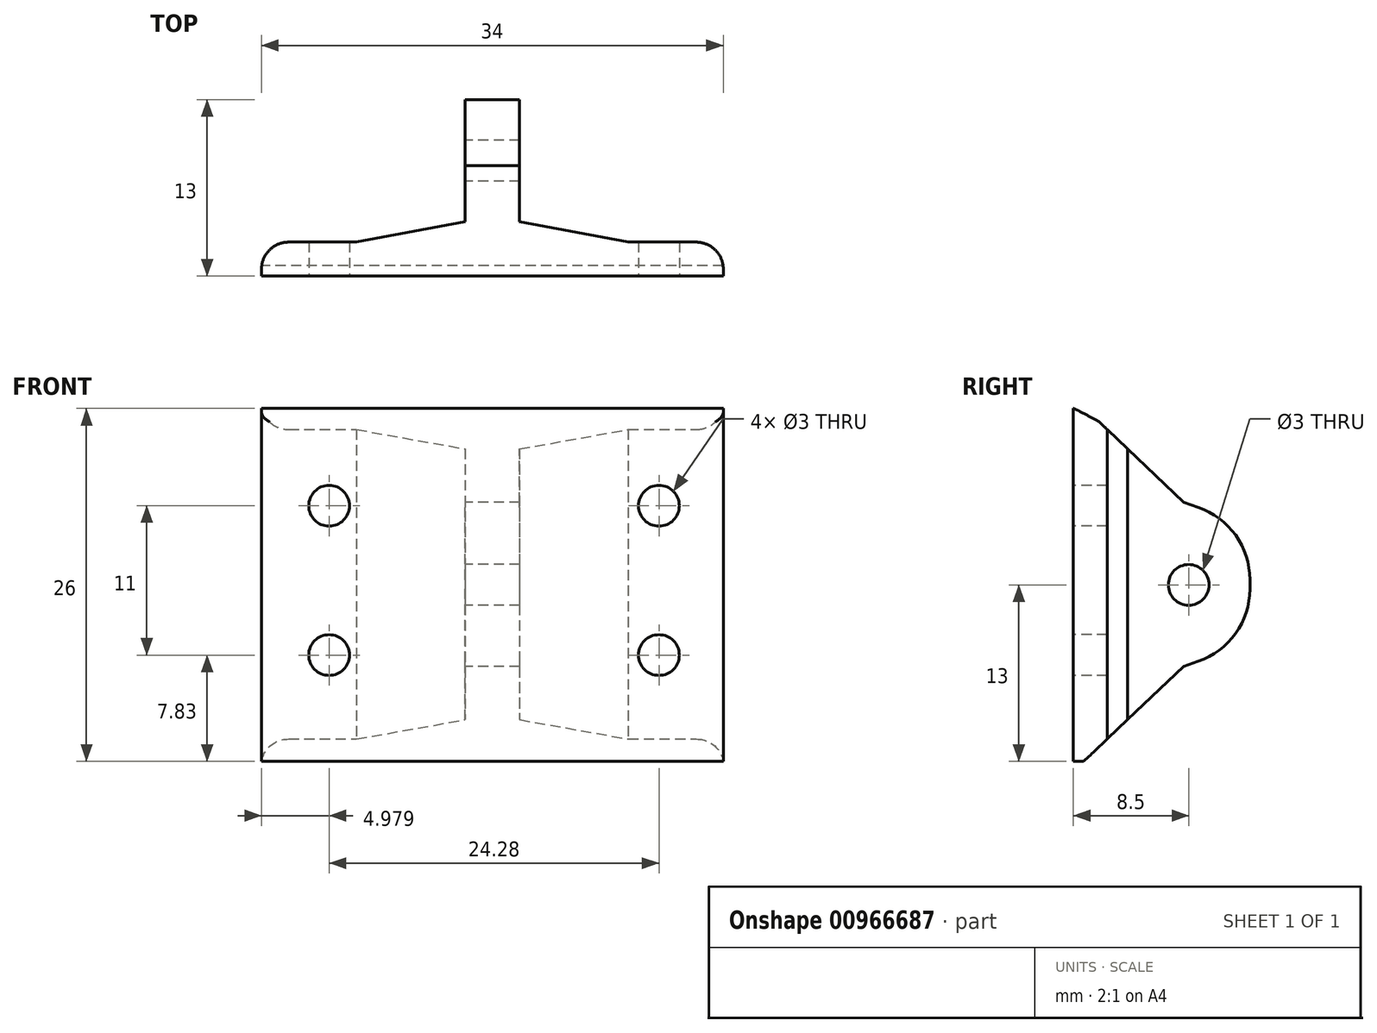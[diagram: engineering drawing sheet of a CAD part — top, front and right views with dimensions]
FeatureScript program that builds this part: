
annotation { "Feature Type Name" : "Feature", "Feature Type Description" : "" }
export const myFeature = defineFeature(function(context is Context, id is Id, definition is map)
    precondition{}
    {
        {
            var Q0;
            Q0=qCreatedBy(makeId("Top.planeOp"),FACE);
            var sketch = newSketch(context, id + "F0", { "sketchPlane" : qUnion([Q0])});
            skLineSegment(sketch, "E0", {"start": v(0, 0) * mm, "end": v(34, 0) * mm});
            skLineSegment(sketch, "E1", {"start": v(34, 0) * mm, "end": v(34, 2.5) * mm});
            skLineSegment(sketch, "E2", {"start": v(19, 4) * mm, "end": v(19, 13) * mm});
            skLineSegment(sketch, "E3", {"start": v(19, 13) * mm, "end": v(15, 13) * mm});
            skLineSegment(sketch, "E4", {"start": v(0, 2.5) * mm, "end": v(0, 0) * mm});
            skLineSegment(sketch, "E5", {"start": v(15, 13) * mm, "end": v(15, 4) * mm});
            skLineSegment(sketch, "E6", {"start": v(15, 4) * mm, "end": v(7, 2.5) * mm});
            skLineSegment(sketch, "E7", {"start": v(7, 2.5) * mm, "end": v(0, 2.5) * mm});
            skLineSegment(sketch, "E8", {"start": v(34, 2.5) * mm, "end": v(27, 2.5) * mm});
            skLineSegment(sketch, "E9", {"start": v(27, 2.5) * mm, "end": v(19, 4) * mm});
            skLineSegment(sketch, "E10", {"start": v(15, 4) * mm, "end": v(19, 4) * mm});
            skSolve(sketch);
        }
        {
            var Q0;
            Q0=qSketchRegion(id+"F0",true);
            var Q1;
            Q1=qSketchRegion(id+"F2",true);
            extrude(context, id + "F1", {"entities" : qUnion([Q0, Q1]), "depth" : 26 * mm, "offsetDistance" : 25 * mm});
        }
        {
            var Q0;
            Q0=qCreatedBy(makeId("Right.planeOp"),FACE);
            var sketch = newSketch(context, id + "F2", { "sketchPlane" : qUnion([Q0])});
            skLineSegment(sketch, "E11", {"start": v(14, 17.06) * mm, "end": v(8.13, 19.08) * mm});
            skLineSegment(sketch, "E12", {"start": v(8.13, 19.08) * mm, "end": v(0.77, 26.1) * mm});
            skLineSegment(sketch, "E13", {"start": v(14, 9) * mm, "end": v(8.13, 7) * mm});
            skLineSegment(sketch, "E14", {"start": v(8.13, 7) * mm, "end": v(0.77, 0) * mm});
            skLineSegment(sketch, "E15", {"start": v(0.77, 0) * mm, "end": v(14, 0) * mm});
            skLineSegment(sketch, "E16", {"start": v(14, 0) * mm, "end": v(14, 9) * mm});
            skLineSegment(sketch, "E17", {"start": v(14, 17.06) * mm, "end": v(14, 26.06) * mm});
            skLineSegment(sketch, "E18", {"start": v(14, 26.06) * mm, "end": v(0.77, 26.1) * mm});
            skSolve(sketch);
        }
        {
            var Q0;
            Q0=makeQuery(id+"F1.opExtrude","SWEPT_FACE",FACE,{"disambiguationData":[OSD([sQuery(id+"F0.wireOp",EDGE,"E5")])]});
            var sketch = newSketch(context, id + "F3", { "sketchPlane" : qUnion([Q0])});
            skPoint(sketch, "E19", {"position": v(-8.5, 13) * mm});
            skPoint(sketch, "E19.positionSnap0", {"position": v(-8.5, 0) * mm});
            skPoint(sketch, "E19.positionSnap1", {"position": v(-4, 13) * mm});
            skSolve(sketch);
        }
        {
            var Q0;
            Q0=qSketchRegion(id+"F2",true);
            extrude(context, id + "F4", {"entities" : qUnion([Q0]), "operationType" : NewBodyOperationType.REMOVE, "depth" : 39 * mm, "offsetDistance" : 25 * mm});
        }
        {
            var Q0;
            Q0=sQuery(id+"F3.wireOp",VERTEX,"E19");
            var Q1;
            Q1=makeQuery(id+"F1.opExtrude","SWEPT_BODY",BODY,{"disambiguationData":[OSD([sQuery(id+"F0.wireOp",EDGE,"E0"),sQuery(id+"F0.wireOp",EDGE,"E1"),sQuery(id+"F0.wireOp",EDGE,"E2"),sQuery(id+"F0.wireOp",EDGE,"E3"),sQuery(id+"F0.wireOp",EDGE,"E4"),sQuery(id+"F0.wireOp",EDGE,"E5"),sQuery(id+"F0.wireOp",EDGE,"E6"),sQuery(id+"F0.wireOp",EDGE,"E7"),sQuery(id+"F0.wireOp",EDGE,"E8"),sQuery(id+"F0.wireOp",EDGE,"E9")])]});
            hole(context, id + "F5", {"style" : HoleStyle.SIMPLE, "endStyle" : HoleEndStyle.THROUGH, "holeDiameter" : 3 * mm, "majorDiameter" : 5 * mm, "isTappedThrough" : true, "tappedDepth" : 12 * mm, "tapClearance" : 3, "locations" : qUnion([Q0]), "scope" : qUnion([Q1])});
        }
        {
            var Q0;
            Q0=makeQuery(id+"F4.boolean.opBoolean","COPY",EDGE,{"derivedFrom":makeQuery(id+"F4.opExtrude","SWEPT_EDGE",EDGE,{"disambiguationData":[OSD([sQuery(id+"F2.wireOp",EDGE,"E14"),sQuery(id+"F2.wireOp",EDGE,"E15")])]})});
            var Q1;
            Q1=makeQuery(id+"F4.boolean.opBoolean","INTERSECT",EDGE,{"derivedFrom":[makeQuery(id+"F1.opExtrude","CAP_FACE",FACE,{"disambiguationData":[OSD([sQuery(id+"F0.wireOp",EDGE,"E0"),sQuery(id+"F0.wireOp",EDGE,"E1"),sQuery(id+"F0.wireOp",EDGE,"E2"),sQuery(id+"F0.wireOp",EDGE,"E3"),sQuery(id+"F0.wireOp",EDGE,"E4"),sQuery(id+"F0.wireOp",EDGE,"E5"),sQuery(id+"F0.wireOp",EDGE,"E6"),sQuery(id+"F0.wireOp",EDGE,"E7"),sQuery(id+"F0.wireOp",EDGE,"E8"),sQuery(id+"F0.wireOp",EDGE,"E9")])],"isStart":false}),makeQuery(id+"F4.opExtrude","SWEPT_FACE",FACE,{"disambiguationData":[OSD([sQuery(id+"F2.wireOp",EDGE,"E12")])]})]});
            fillet(context, id + "F6", {"entities" : qUnion([Q0, Q1]), "radius" : 4 * mm, "tangentPropagation" : true, "rho" : 0.1, "crossSection" : FilletCrossSection.CONIC, "allowEdgeOverflow" : false});
        }
        {
            var Q0;
            Q0=makeQuery(id+"F1.opExtrude","SWEPT_EDGE",EDGE,{"disambiguationData":[OSD([sQuery(id+"F0.wireOp",EDGE,"E4"),sQuery(id+"F0.wireOp",EDGE,"E7")])]});
            var Q1;
            Q1=makeQuery(id+"F1.opExtrude","SWEPT_EDGE",EDGE,{"disambiguationData":[OSD([sQuery(id+"F0.wireOp",EDGE,"E1"),sQuery(id+"F0.wireOp",EDGE,"E8")])]});
            fillet(context, id + "F7", {"entities" : qUnion([Q0, Q1]), "radius" : 2 * mm, "tangentPropagation" : true, "allowEdgeOverflow" : false});
        }
        {
            var Q0;
            Q0=qCreatedBy(makeId("Front.planeOp"),FACE);
            var sketch = newSketch(context, id + "F8", { "sketchPlane" : qUnion([Q0])});
            skPoint(sketch, "E20", {"position": v(29.26, 18.83) * mm});
            skPoint(sketch, "E21", {"position": v(29.26, 7.83) * mm});
            skPoint(sketch, "E22", {"position": v(4.98, 7.83) * mm});
            skPoint(sketch, "E23", {"position": v(4.98, 18.83) * mm});
            skSolve(sketch);
        }
        {
            var Q0;
            Q0=sQuery(id+"F8.wireOp",VERTEX,"bc9bccba-1599-442e-bb94-a080d1391aad");
            var Q1;
            Q1=sQuery(id+"F8.wireOp",VERTEX,"E20");
            var Q2;
            Q2=sQuery(id+"F8.wireOp",VERTEX,"E21");
            var Q3;
            Q3=sQuery(id+"F8.wireOp",VERTEX,"8df3dbca-8a22-420a-a98d-48ef7003d5ff");
            var Q4;
            Q4=sQuery(id+"F8.wireOp",VERTEX,"E23");
            var Q5;
            Q5=sQuery(id+"F8.wireOp",VERTEX,"E22");
            var Q6;
            Q6=makeQuery(id+"F1.opExtrude","SWEPT_BODY",BODY,{"disambiguationData":[OSD([sQuery(id+"F0.wireOp",EDGE,"E0"),sQuery(id+"F0.wireOp",EDGE,"E1"),sQuery(id+"F0.wireOp",EDGE,"E2"),sQuery(id+"F0.wireOp",EDGE,"E3"),sQuery(id+"F0.wireOp",EDGE,"E4"),sQuery(id+"F0.wireOp",EDGE,"E5"),sQuery(id+"F0.wireOp",EDGE,"E6"),sQuery(id+"F0.wireOp",EDGE,"E7"),sQuery(id+"F0.wireOp",EDGE,"E8"),sQuery(id+"F0.wireOp",EDGE,"E9")])]});
            hole(context, id + "F9", {"style" : HoleStyle.SIMPLE, "endStyle" : HoleEndStyle.THROUGH, "holeDiameter" : 3 * mm, "majorDiameter" : 5 * mm, "isTappedThrough" : true, "tappedDepth" : 12 * mm, "tapClearance" : 3, "locations" : qUnion([Q0, Q1, Q2, Q3, Q4, Q5]), "scope" : qUnion([Q6])});
        }
        {
            var Q0;
            Q0=makeQuery(id+"F4.boolean.opBoolean","INTERSECT",EDGE,{"derivedFrom":[makeQuery(id+"F1.opExtrude","SWEPT_FACE",FACE,{"disambiguationData":[OSD([sQuery(id+"F0.wireOp",EDGE,"E3")])]}),makeQuery(id+"F4.opExtrude","SWEPT_FACE",FACE,{"disambiguationData":[OSD([sQuery(id+"F2.wireOp",EDGE,"E11")])]})]});
            var Q1;
            Q1=makeQuery(id+"F4.boolean.opBoolean","INTERSECT",EDGE,{"derivedFrom":[makeQuery(id+"F1.opExtrude","SWEPT_FACE",FACE,{"disambiguationData":[OSD([sQuery(id+"F0.wireOp",EDGE,"E3")])]}),makeQuery(id+"F4.opExtrude","SWEPT_FACE",FACE,{"disambiguationData":[OSD([sQuery(id+"F2.wireOp",EDGE,"E13")])]})]});
            fillet(context, id + "F10", {"entities" : qUnion([Q0, Q1]), "radius" : 5.63 * mm, "tangentPropagation" : true, "allowEdgeOverflow" : false});
        }
    });
